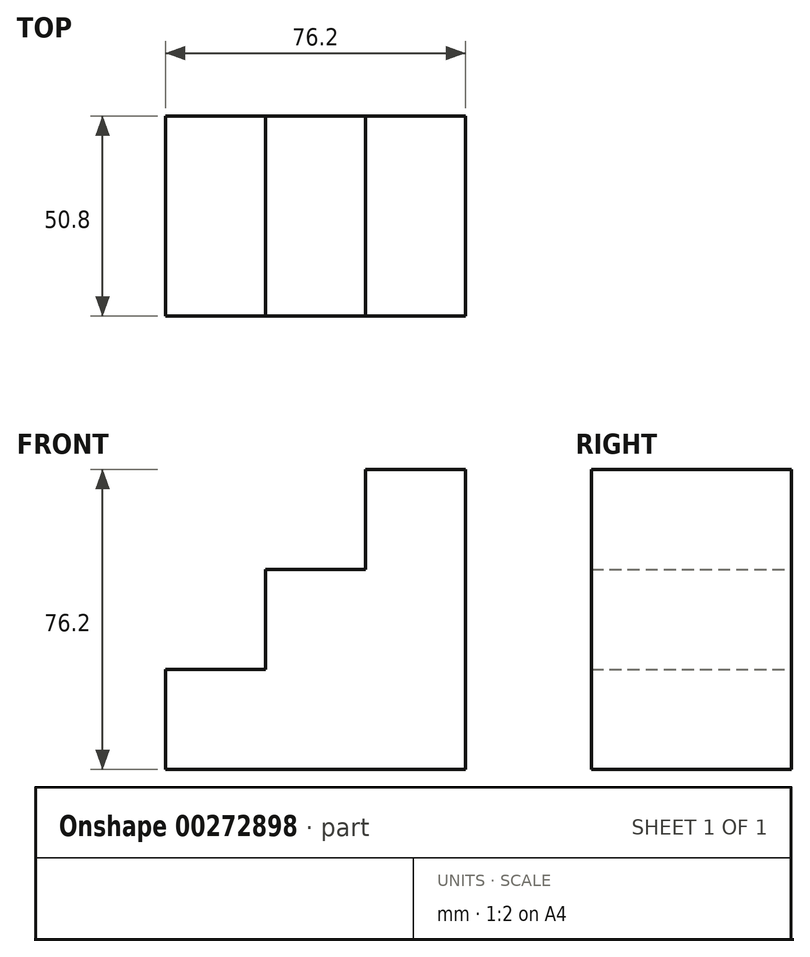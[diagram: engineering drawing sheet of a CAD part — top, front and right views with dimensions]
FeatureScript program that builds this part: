
annotation { "Feature Type Name" : "Feature", "Feature Type Description" : "" }
export const myFeature = defineFeature(function(context is Context, id is Id, definition is map)
    precondition{}
    {
        {
            var Q0;
            Q0=qCreatedBy(makeId("Front.planeOp"),FACE);
            var sketch = newSketch(context, id + "F0", { "sketchPlane" : qUnion([Q0])});
            skLineSegment(sketch, "E0", {"start": v(0, 0) * mm, "end": v(0, 76.2) * mm});
            skLineSegment(sketch, "E1", {"start": v(-25.4, 76.2) * mm, "end": v(0, 76.2) * mm});
            skLineSegment(sketch, "E2", {"start": v(-25.4, 76.2) * mm, "end": v(-25.4, 50.8) * mm});
            skLineSegment(sketch, "E3", {"start": v(-50.8, 50.8) * mm, "end": v(-25.4, 50.8) * mm});
            skLineSegment(sketch, "E4", {"start": v(-50.8, 50.8) * mm, "end": v(-50.8, 25.4) * mm});
            skLineSegment(sketch, "E5", {"start": v(-76.2, 25.4) * mm, "end": v(-50.8, 25.4) * mm});
            skLineSegment(sketch, "E6", {"start": v(-76.2, 25.4) * mm, "end": v(-76.2, 0) * mm});
            skLineSegment(sketch, "E7", {"start": v(-76.2, 0) * mm, "end": v(0, 0) * mm});
            skSolve(sketch);
        }
        {
            var Q0;
            Q0 = qSketchRegion(id + "F0", true);
            extrude(context, id + "F1", {"entities" : qUnion([Q0]), "depth" : 50.8 * mm});
        }
    });
